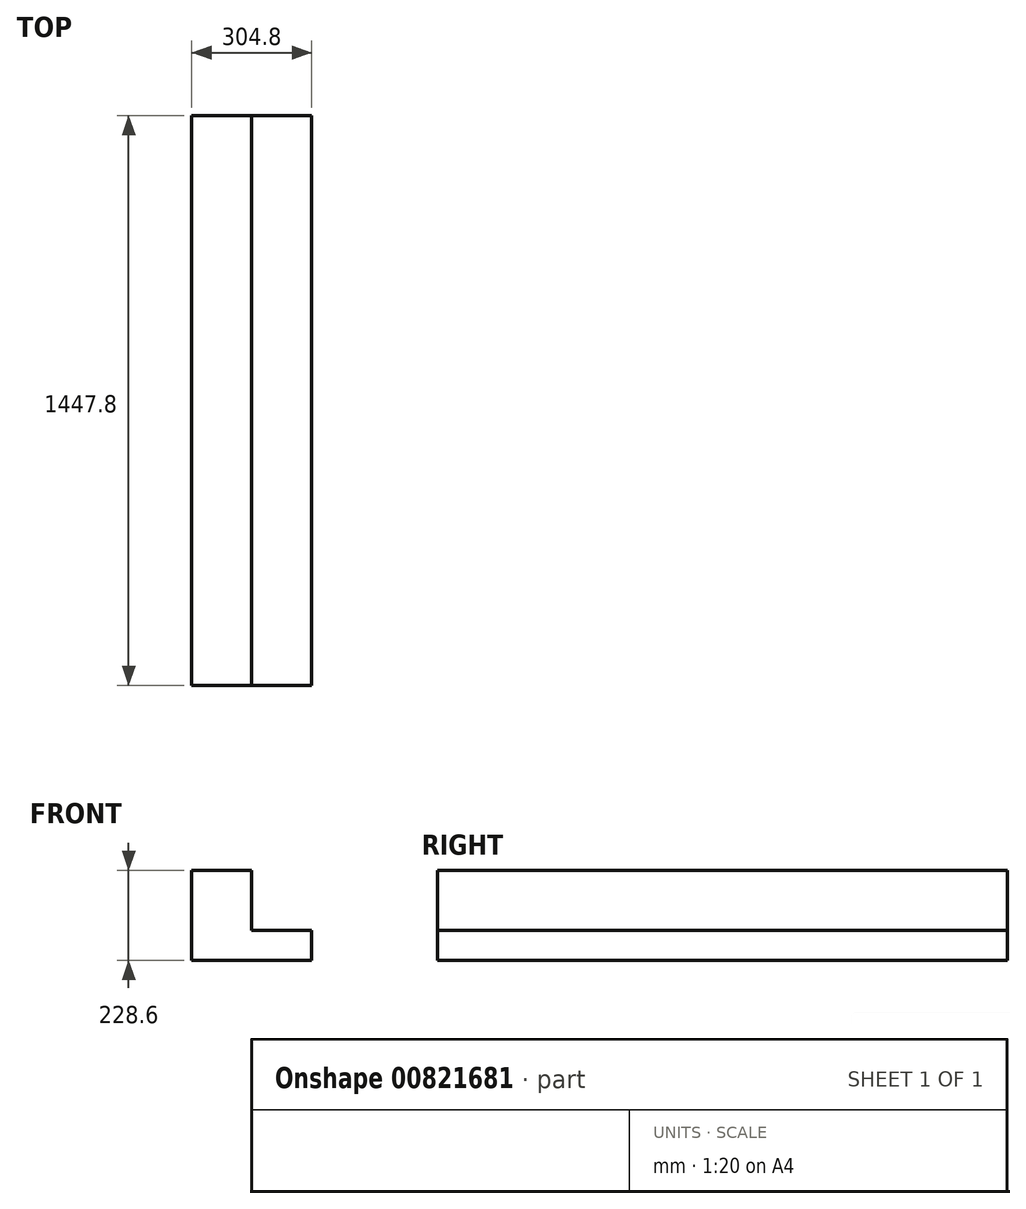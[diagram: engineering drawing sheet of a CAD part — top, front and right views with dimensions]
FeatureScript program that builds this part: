
annotation { "Feature Type Name" : "Feature", "Feature Type Description" : "" }
export const myFeature = defineFeature(function(context is Context, id is Id, definition is map)
    precondition{}
    {
        {
            var Q0;
            Q0=qCreatedBy(makeId("Front.planeOp"),FACE);
            var sketch = newSketch(context, id + "F0", { "sketchPlane" : qUnion([Q0])});
            skLineSegment(sketch, "E0", {"start": v(0, 0) * mm, "end": v(0, 76.2) * mm});
            skLineSegment(sketch, "E1", {"start": v(0, 76.2) * mm, "end": v(-152.4, 76.2) * mm});
            skLineSegment(sketch, "E2", {"start": v(-152.4, 76.2) * mm, "end": v(-152.4, 228.6) * mm});
            skLineSegment(sketch, "E3", {"start": v(-152.4, 228.6) * mm, "end": v(-304.8, 228.6) * mm});
            skLineSegment(sketch, "E4", {"start": v(-304.8, 228.6) * mm, "end": v(-304.8, 0) * mm});
            skLineSegment(sketch, "E5", {"start": v(-304.8, 0) * mm, "end": v(0, 0) * mm});
            skSolve(sketch);
        }
        {
            var Q0;
            Q0 = qSketchRegion(id + "F0", true);
            extrude(context, id + "F1", {"entities" : qUnion([Q0]), "depth" : 1447.8 * mm, "offsetDistance" : 25.4 * mm});
        }
    });
